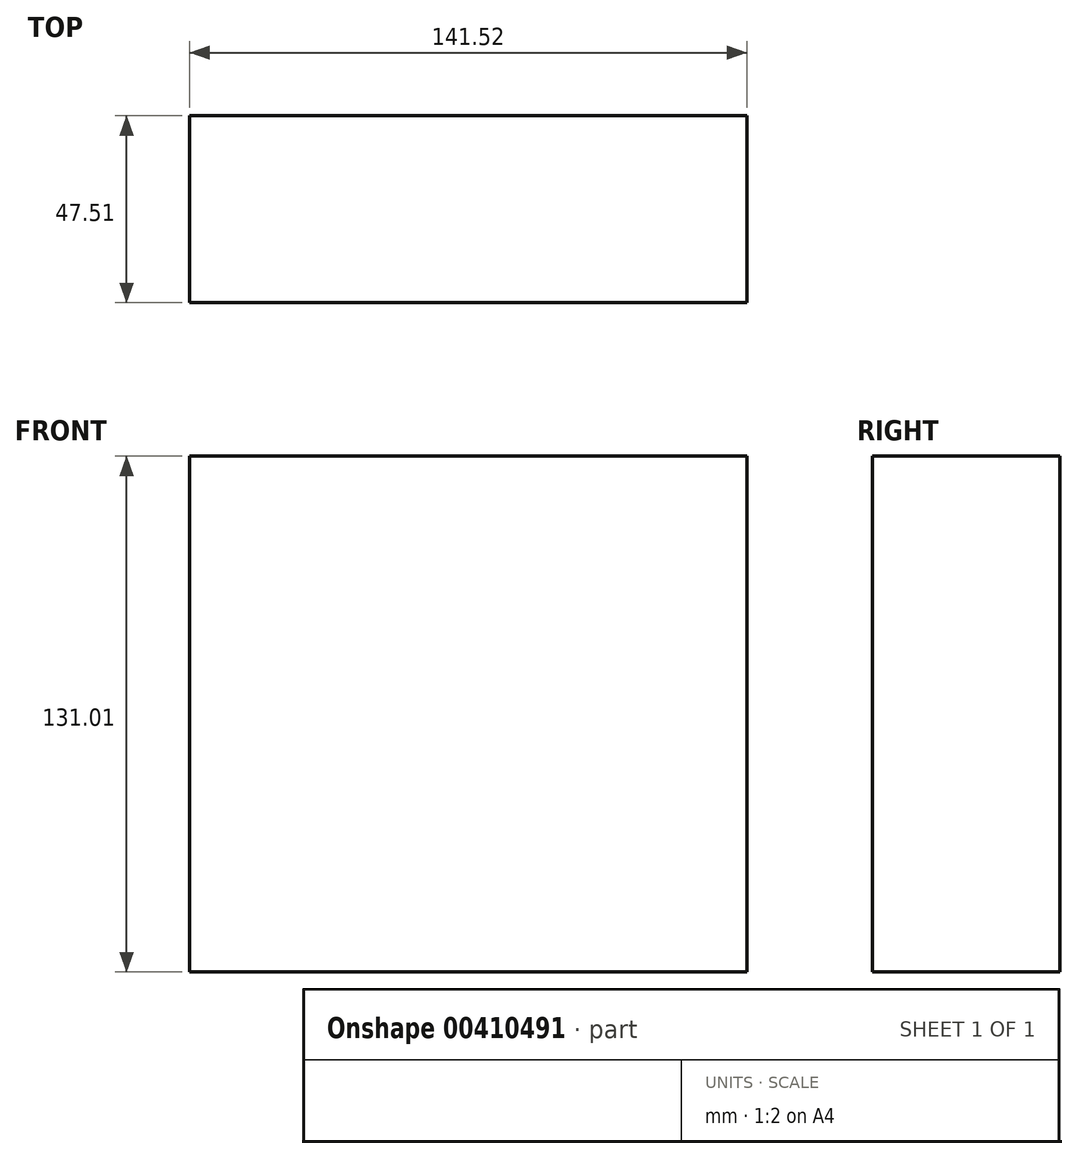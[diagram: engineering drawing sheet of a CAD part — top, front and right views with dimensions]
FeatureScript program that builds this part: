
annotation { "Feature Type Name" : "Feature", "Feature Type Description" : "" }
export const myFeature = defineFeature(function(context is Context, id is Id, definition is map)
    precondition{}
    {
        {
            var Q0;
            Q0=qCreatedBy(makeId("Front.planeOp"),FACE);
            var sketch = newSketch(context, id + "F0", { "sketchPlane" : qUnion([Q0])});
            skLineSegment(sketch, "E0", {"start": v(0, 0) * mm, "end": v(0, 131) * mm});
            skLineSegment(sketch, "E1.bottom", {"start": v(141.52, 131) * mm, "end": v(0, 131) * mm});
            skLineSegment(sketch, "E1.top", {"start": v(141.52, 0) * mm, "end": v(0, 0) * mm});
            skLineSegment(sketch, "E1.left", {"start": v(141.52, 131) * mm, "end": v(141.52, 0) * mm});
            skLineSegment(sketch, "E1.right", {"start": v(0, 131) * mm, "end": v(0, 0) * mm});
            skSolve(sketch);
        }
        {
            var Q0;
            Q0=makeQuery(id+"F0.imprint","IMPRINT",FACE,{"disambiguationData":[TD([[makeQuery(id+"F0.imprint","IMPRINT",EDGE,{"derivedFrom":sQuery(id+"F0.wireOp",EDGE,"E1.bottom")}),1.0]])]});
            extrude(context, id + "F1", {"entities" : qUnion([Q0]), "depth" : 47.5 * mm});
        }
    });
